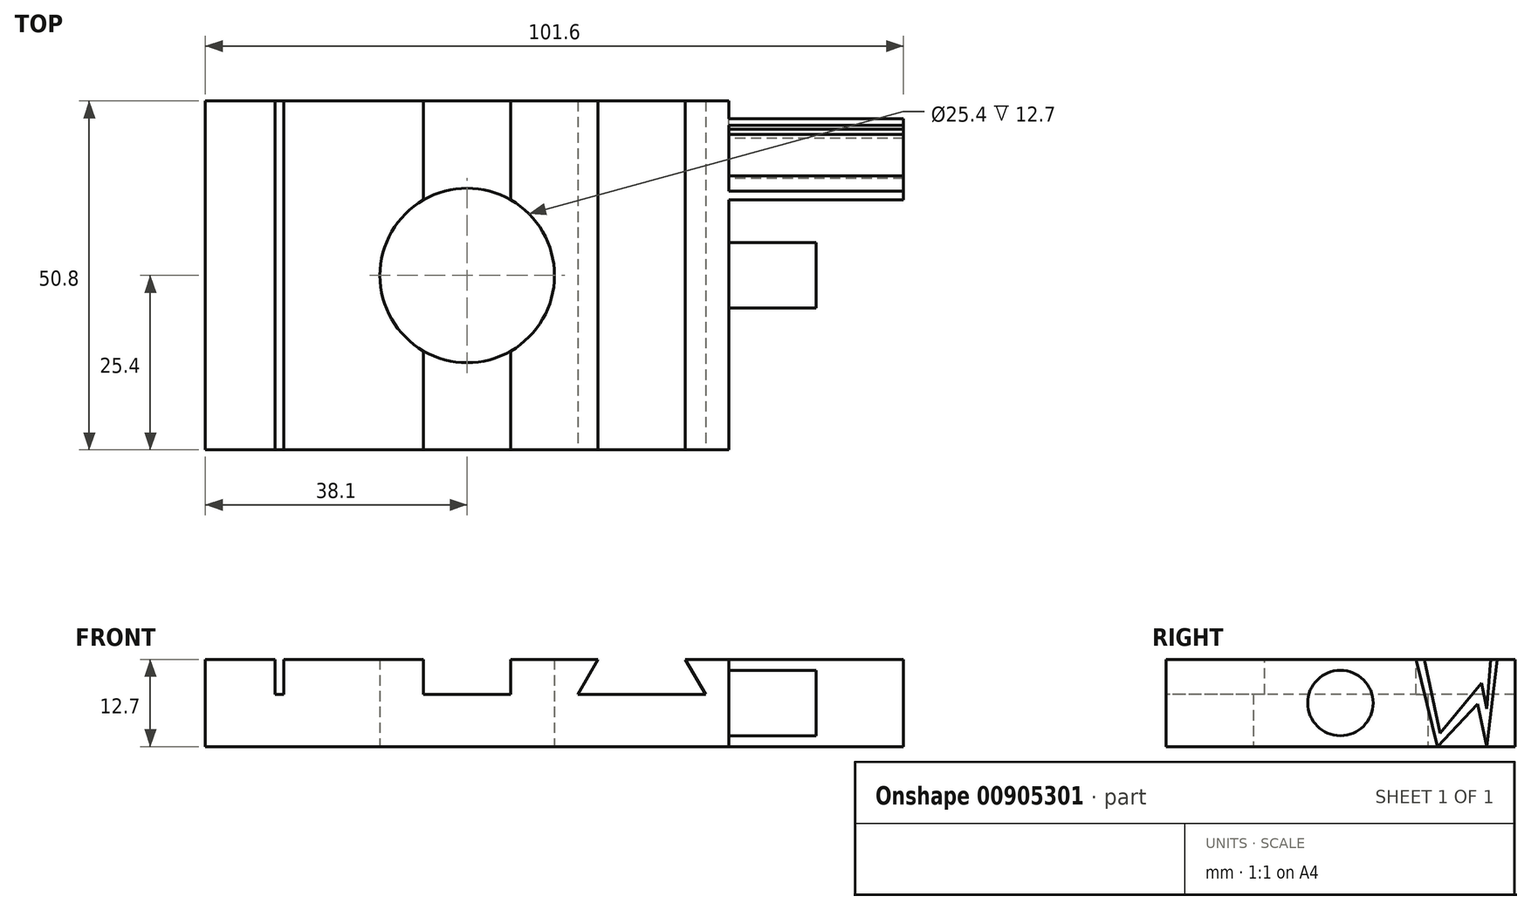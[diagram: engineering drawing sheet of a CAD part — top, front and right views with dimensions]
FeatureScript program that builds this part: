
annotation { "Feature Type Name" : "Feature", "Feature Type Description" : "" }
export const myFeature = defineFeature(function(context is Context, id is Id, definition is map)
    precondition{}
    {
        {
            var Q0;
            Q0=qCreatedBy(makeId("Top.planeOp"),FACE);
            var sketch = newSketch(context, id + "F0", { "sketchPlane" : qUnion([Q0])});
            skLineSegment(sketch, "E0.bottom", {"start": v(38.1, 25.4) * mm, "end": v(-38.1, 25.4) * mm});
            skLineSegment(sketch, "E0.top", {"start": v(38.1, -25.4) * mm, "end": v(-38.1, -25.4) * mm});
            skLineSegment(sketch, "E0.left", {"start": v(38.1, 25.4) * mm, "end": v(38.1, -25.4) * mm});
            skLineSegment(sketch, "E0.right", {"start": v(-38.1, 25.4) * mm, "end": v(-38.1, -25.4) * mm});
            skPoint(sketch, "E0.middle", {"position": v(0, 0) * mm});
            skCircle(sketch, "E1", {"center": v(0, 0) * mm, "radius": 12.7 * mm});
            skSolve(sketch);
        }
        {
            var Q0;
            Q0=makeQuery(id+"F0.imprint","IMPRINT",FACE,{"disambiguationData":[TD([[makeQuery(id+"F0.imprint","IMPRINT",EDGE,{"derivedFrom":sQuery(id+"F0.wireOp",EDGE,"E0.bottom")}),1.0]])]});
            extrude(context, id + "F1", {"entities" : qUnion([Q0]), "depth" : 12.7 * mm, "offsetDistance" : 25.4 * mm});
        }
        {
            var Q0;
            Q0=makeQuery(id+"F1.opExtrude","CAP_FACE",FACE,{"disambiguationData":[OSD([sQuery(id+"F0.wireOp",EDGE,"E0.bottom"),sQuery(id+"F0.wireOp",EDGE,"E0.top"),sQuery(id+"F0.wireOp",EDGE,"E0.left"),sQuery(id+"F0.wireOp",EDGE,"E0.right"),sQuery(id+"F0.wireOp",EDGE,"E1")])],"isStart":false});
            var sketch = newSketch(context, id + "F2", { "sketchPlane" : qUnion([Q0])});
            skLineSegment(sketch, "E2.bottom", {"start": v(-27.94, 25.4) * mm, "end": v(-26.67, 25.4) * mm});
            skLineSegment(sketch, "E2.top", {"start": v(-27.94, -25.4) * mm, "end": v(-26.67, -25.4) * mm});
            skLineSegment(sketch, "E2.left", {"start": v(-27.94, 25.4) * mm, "end": v(-27.94, -25.4) * mm});
            skLineSegment(sketch, "E2.right", {"start": v(-26.67, 25.4) * mm, "end": v(-26.67, -25.4) * mm});
            skLineSegment(sketch, "E3", {"start": v(-6.35, 25.4) * mm, "end": v(-6.35, -25.4) * mm});
            skLineSegment(sketch, "E4", {"start": v(-6.35, -25.4) * mm, "end": v(6.35, -25.4) * mm});
            skLineSegment(sketch, "E5", {"start": v(6.35, -25.4) * mm, "end": v(6.35, 25.4) * mm});
            skLineSegment(sketch, "E6", {"start": v(6.35, 25.4) * mm, "end": v(-6.35, 25.4) * mm});
            skPoint(sketch, "E7", {"position": v(0, 0) * mm});
            skLineSegment(sketch, "E8", {"start": v(0, 25.4) * mm, "end": v(0, -25.4) * mm, "construction": true});
            skSolve(sketch);
        }
        {
            var Q0;
            Q0=makeQuery(id+"F2.imprint","IMPRINT",FACE,{"disambiguationData":[TD([[makeQuery(id+"F2.imprint","IMPRINT",EDGE,{"derivedFrom":sQuery(id+"F2.wireOp",EDGE,"E2.bottom")}),1.0]])]});
            var Q1;
            {var subQ0=sQuery(id+"F2.wireOp",EDGE,"E4");Q1=makeQuery(id+"F2.imprint","IMPRINT",FACE,{"disambiguationData":[TD([[makeQuery(id+"F2.imprint","IMPRINT",EDGE,{"derivedFrom":subQ0}),-1.0]])]});}
            var Q2;
            {var subQ0=sQuery(id+"F2.wireOp",EDGE,"E6");Q2=makeQuery(id+"F2.imprint","IMPRINT",FACE,{"disambiguationData":[TD([[makeQuery(id+"F2.imprint","IMPRINT",EDGE,{"derivedFrom":subQ0}),1.0]])]});}
            extrude(context, id + "F3", {"entities" : qUnion([Q0, Q1, Q2]), "operationType" : NewBodyOperationType.REMOVE, "oppositeDirection" : true, "depth" : 5.08 * mm, "offsetDistance" : 25.4 * mm});
        }
        {
            var Q0;
            Q0=makeQuery(id+"F1.opExtrude","SWEPT_FACE",FACE,{"disambiguationData":[OSD([sQuery(id+"F0.wireOp",EDGE,"E0.top")])]});
            var sketch = newSketch(context, id + "F4", { "sketchPlane" : qUnion([Q0])});
            skLineSegment(sketch, "E9", {"start": v(19.05, 12.7) * mm, "end": v(16.12, 7.62) * mm});
            skLineSegment(sketch, "E10", {"start": v(16.12, 7.62) * mm, "end": v(34.68, 7.62) * mm});
            skLineSegment(sketch, "E11", {"start": v(34.68, 7.62) * mm, "end": v(31.75, 12.7) * mm});
            skLineSegment(sketch, "E12", {"start": v(31.75, 12.7) * mm, "end": v(19.05, 12.7) * mm});
            skLineSegment(sketch, "E13", {"start": v(25.4, 7.62) * mm, "end": v(25.4, 12.7) * mm, "construction": true});
            skSolve(sketch);
        }
        {
            var Q0;
            Q0=makeQuery(id+"F4.imprint","IMPRINT",FACE,{"disambiguationData":[TD([[makeQuery(id+"F4.imprint","IMPRINT",EDGE,{"derivedFrom":sQuery(id+"F4.wireOp",EDGE,"E9")}),1.0]])]});
            extrude(context, id + "F5", {"entities" : qUnion([Q0]), "operationType" : NewBodyOperationType.REMOVE, "endBound" : BoundingType.THROUGH_ALL, "oppositeDirection" : true, "depth" : 25.4 * mm, "offsetDistance" : 25.4 * mm});
        }
        {
            var Q0;
            Q0=makeQuery(id+"F1.opExtrude","SWEPT_FACE",FACE,{"disambiguationData":[OSD([sQuery(id+"F0.wireOp",EDGE,"E0.left")])]});
            var sketch = newSketch(context, id + "F6", { "sketchPlane" : qUnion([Q0])});
            skCircle(sketch, "E14", {"center": v(0, 6.35) * mm, "radius": 4.76 * mm});
            skPoint(sketch, "E14.centerSnap0", {"position": v(-25.4, 6.35) * mm});
            skSolve(sketch);
        }
        {
            var Q0;
            Q0=makeQuery(id+"F6.imprint","IMPRINT",FACE,{"disambiguationData":[TD([[makeQuery(id+"F6.imprint","IMPRINT",EDGE,{"derivedFrom":sQuery(id+"F6.wireOp",EDGE,"E14")}),1.0]])]});
            extrude(context, id + "F7", {"entities" : qUnion([Q0]), "operationType" : NewBodyOperationType.ADD, "depth" : 12.7 * mm, "offsetDistance" : 25.4 * mm});
        }
        {
            var Q0;
            Q0=makeQuery(id+"F1.opExtrude","SWEPT_FACE",FACE,{"disambiguationData":[OSD([sQuery(id+"F0.wireOp",EDGE,"E0.left")])]});
            var sketch = newSketch(context, id + "F8", { "sketchPlane" : qUnion([Q0])});
            skLineSegment(sketch, "E15", {"start": v(11, 12.7) * mm, "end": v(14.11, 0) * mm});
            skLineSegment(sketch, "E16", {"start": v(14.11, 0) * mm, "end": v(20, 6.2) * mm});
            skLineSegment(sketch, "E17", {"start": v(20, 6.2) * mm, "end": v(21.3, 0) * mm});
            skLineSegment(sketch, "E18", {"start": v(21.3, 0) * mm, "end": v(22.81, 12.7) * mm});
            skLineSegment(sketch, "E19", {"start": v(22.81, 12.7) * mm, "end": v(21.87, 12.7) * mm});
            skLineSegment(sketch, "E20", {"start": v(21.87, 12.7) * mm, "end": v(21.3, 5.51) * mm});
            skLineSegment(sketch, "E21", {"start": v(21.3, 5.51) * mm, "end": v(20.52, 9.25) * mm});
            skLineSegment(sketch, "E22", {"start": v(20.52, 9.25) * mm, "end": v(14.52, 1.92) * mm});
            skLineSegment(sketch, "E23", {"start": v(14.52, 1.92) * mm, "end": v(12.25, 12.7) * mm});
            skLineSegment(sketch, "E24", {"start": v(12.25, 12.7) * mm, "end": v(11, 12.7) * mm});
            skSolve(sketch);
        }
        {
            var Q0;
            Q0=makeQuery(id+"F8.imprint","IMPRINT",FACE,{"disambiguationData":[TD([[makeQuery(id+"F8.imprint","IMPRINT",EDGE,{"derivedFrom":sQuery(id+"F8.wireOp",EDGE,"E15")}),1.0]])]});
            extrude(context, id + "F9", {"entities" : qUnion([Q0]), "operationType" : NewBodyOperationType.ADD, "depth" : 25.4 * mm, "offsetDistance" : 25.4 * mm});
        }
    });
